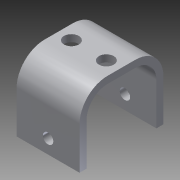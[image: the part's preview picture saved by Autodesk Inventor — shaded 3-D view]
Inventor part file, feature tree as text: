
AUTODESK INVENTOR PART (.ipt)
format: ipt  version: 2013 (Build 170138000, 138)  size: 169,472 bytes
history: native  units: in
note: dims shown in document units (in); Inventor stores cm internally (conversion verified against a paired STEP export)
features: sheet_metal_op x7, sketch x7, other x5, projected_geometry x1
ambient origin geometry x8: Origin, YZ Plane, XZ Plane, XY Plane, X Axis, Y Axis, Z Axis, Center Point
bodies: Solid1 (feature_tree)
feature tree (20):
  sheet_metal_op  "Face1"
  sheet_metal_op  "Flange3"
  sheet_metal_op  "Flange4"
  sketch  "Sketch9"  dims[d29=0.125in]
  sketch  "Sketch10"  dims[d30=0.0625in d31=0.25in d32=0.125in d33=1.0in d34=90.0deg d35=0.375in d36=0.5in d37=0.125in d38=0.125in d39=0.125in d40=0.0625in d41=0.25in d42=0.125in d43=1.25in d44=90.0deg d45=0.375in d46=0.5in d47=0.125in d48=0.125in d49=0.125in d50=0.0in d51=0.25in d52=0.266in d53=0.25in d54=0.266in d55=0.125in d56=0.0in]
  sketch  "Sketch1"  dims[d0=1.125in]
  other  "Plate1"
  sketch  "Sketch5"  dims[d1=0.75in]
  other  "Plate4"
  sheet_metal_op  "Bend3"
  sheet_metal_op  "Corner3"
  sketch  "Sketch6"  dims[d2=0.25in]
  other  "Plate5"
  sheet_metal_op  "Bend4"
  sheet_metal_op  "Corner4"
  sketch  "Sketch7"  dims[d3=0.1875in]
  projected_geometry  "Projected Loop1"
  sketch  "Sketch8"  dims[d4=0.125in]
  other  "Cut2"
  other  "Cut3"
